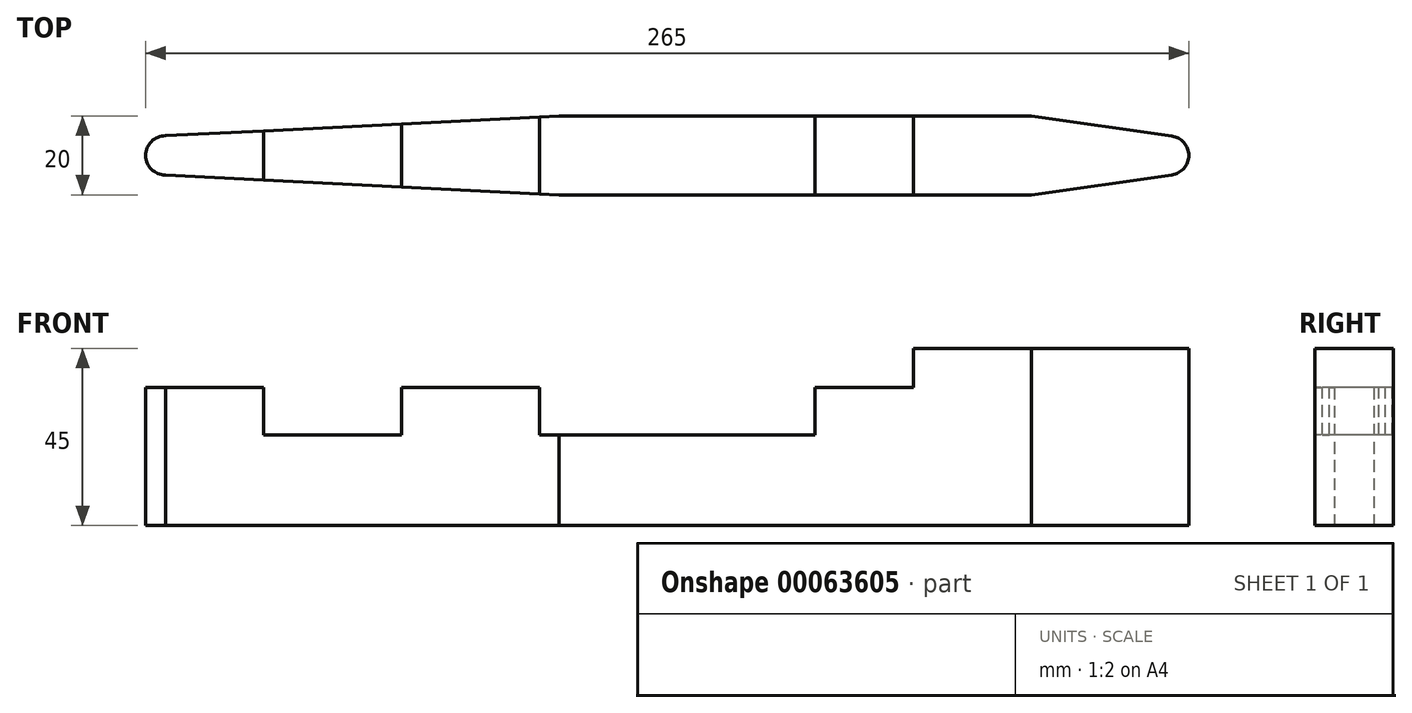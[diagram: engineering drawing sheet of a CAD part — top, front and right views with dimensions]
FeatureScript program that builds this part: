
annotation { "Feature Type Name" : "Feature", "Feature Type Description" : "" }
export const myFeature = defineFeature(function(context is Context, id is Id, definition is map)
    precondition{}
    {
        {
            var Q0;
            Q0=qCreatedBy(makeId("Top.planeOp"),FACE);
            var sketch = newSketch(context, id + "F0", { "sketchPlane" : qUnion([Q0])});
            skLineSegment(sketch, "E0.bottom", {"start": v(57.18, -9.81) * mm, "end": v(-62.82, -9.81) * mm});
            skPoint(sketch, "E0.middle", {"position": v(-35.32, 0.19) * mm});
            skLineSegment(sketch, "E1", {"start": v(-167.82, 0.19) * mm, "end": v(97.18, 0.19) * mm, "construction": true});
            skLineSegment(sketch, "E2", {"start": v(-62.82, 17.45) * mm, "end": v(-62.82, -22.54) * mm, "construction": true});
            skLineSegment(sketch, "E3", {"start": v(57.18, 19.18) * mm, "end": v(57.18, -20.82) * mm, "construction": true});
            skArc(sketch, "E4", {"start": v(-162.82, 5.19) * mm, "mid": v(-167.82, 0.19) * mm, "end": v(-162.82, -4.81) * mm});
            skLineSegment(sketch, "E5", {"start": v(-62.82, -9.81) * mm, "end": v(-162.82, -4.81) * mm});
            skLineSegment(sketch, "E6", {"start": v(57.18, 10.19) * mm, "end": v(92.88, 5.14) * mm});
            skLineSegment(sketch, "E7", {"start": v(57.18, -9.81) * mm, "end": v(92.88, -4.76) * mm});
            skPoint(sketch, "E8.orphan", {"position": v(97.18, 10.19) * mm});
            skPoint(sketch, "E9.orphan", {"position": v(97.18, -9.81) * mm});
            skLineSegment(sketch, "E10", {"start": v(57.18, 10.19) * mm, "end": v(-62.82, 10.19) * mm});
            skLineSegment(sketch, "E11", {"start": v(-62.82, 10.19) * mm, "end": v(-162.82, 5.19) * mm});
            skPoint(sketch, "E12.orphan", {"position": v(-167.82, 10.19) * mm});
            skPoint(sketch, "E0.right.start.orphan", {"position": v(-167.82, -9.81) * mm});
            skLineSegment(sketch, "E13.trimOffspring", {"start": v(92.18, -4.81) * mm, "end": v(92.18, -4.86) * mm, "construction": true});
            skLineSegment(sketch, "E14", {"start": v(92.18, -4.86) * mm, "end": v(92.88, -4.76) * mm});
            skLineSegment(sketch, "E15", {"start": v(97.18, 4.48) * mm, "end": v(97.18, 0.19) * mm});
            skLineSegment(sketch, "E16", {"start": v(97.18, 4.48) * mm, "end": v(97.18, 4.53) * mm});
            skArc(sketch, "E17", {"start": v(92.88, -4.76) * mm, "mid": v(97.18, 0.19) * mm, "end": v(92.88, 5.14) * mm});
            skPoint(sketch, "E18.orphan", {"position": v(92.18, -8.18) * mm});
            skSolve(sketch);
        }
        {
            var Q0;
            Q0=makeQuery(id+"F0.imprint","IMPRINT",FACE,{"disambiguationData":[TD([[makeQuery(id+"F0.imprint","IMPRINT",EDGE,{"derivedFrom":sQuery(id+"F0.wireOp",EDGE,"E0.bottom")}),-1.0]])]});
            extrude(context, id + "F1", {"entities" : qUnion([Q0]), "depth" : 35 * mm});
        }
        {
            var Q0;
            Q0=makeQuery(id+"F1.opExtrude","CAP_FACE",FACE,{"disambiguationData":[OSD([sQuery(id+"F0.wireOp",EDGE,"E0.bottom"),sQuery(id+"F0.wireOp",EDGE,"14d6f1a2-3771-4236-a4c2-8c3a8a42184f"),sQuery(id+"F0.wireOp",EDGE,"E4"),sQuery(id+"F0.wireOp",EDGE,"E5"),sQuery(id+"F0.wireOp",EDGE,"E6"),sQuery(id+"F0.wireOp",EDGE,"E7"),sQuery(id+"F0.wireOp",EDGE,"E10"),sQuery(id+"F0.wireOp",EDGE,"E11")])],"isStart":false});
            var sketch = newSketch(context, id + "F2", { "sketchPlane" : qUnion([Q0])});
            skLineSegment(sketch, "E19", {"start": v(27.18, 10.19) * mm, "end": v(27.18, -9.81) * mm, "construction": true});
            skLineSegment(sketch, "E20", {"start": v(27.18, 10.19) * mm, "end": v(27.18, -9.81) * mm});
            skSolve(sketch);
        }
        {
            var Q0;
            {var subQ2=sQuery(id+"F2.wireOp",EDGE,"E20");Q0=makeQuery(id+"F2.imprint","IMPRINT",FACE,{"disambiguationData":[TD([[makeQuery(id+"F2.imprint","IMPRINT",EDGE,{"derivedFrom":subQ2}),1.0]])]});}
            extrude(context, id + "F3", {"entities" : qUnion([Q0]), "operationType" : NewBodyOperationType.ADD, "depth" : 10 * mm});
        }
        {
            var Q0;
            Q0=makeQuery(id+"F1.opExtrude","CAP_FACE",FACE,{"disambiguationData":[OSD([sQuery(id+"F0.wireOp",EDGE,"E0.bottom"),sQuery(id+"F0.wireOp",EDGE,"14d6f1a2-3771-4236-a4c2-8c3a8a42184f"),sQuery(id+"F0.wireOp",EDGE,"E4"),sQuery(id+"F0.wireOp",EDGE,"E5"),sQuery(id+"F0.wireOp",EDGE,"E6"),sQuery(id+"F0.wireOp",EDGE,"E7"),sQuery(id+"F0.wireOp",EDGE,"E10"),sQuery(id+"F0.wireOp",EDGE,"E11")])],"isStart":false});
            var sketch = newSketch(context, id + "F4", { "sketchPlane" : qUnion([Q0])});
            skLineSegment(sketch, "E21", {"start": v(2.18, 10.19) * mm, "end": v(2.18, -9.81) * mm});
            skLineSegment(sketch, "E22", {"start": v(-67.82, 10.19) * mm, "end": v(-67.82, -9.81) * mm});
            skLineSegment(sketch, "E23", {"start": v(-137.82, 6.44) * mm, "end": v(-137.82, -6.06) * mm});
            skLineSegment(sketch, "E24", {"start": v(-102.82, 8.19) * mm, "end": v(-102.82, -7.81) * mm});
            skSolve(sketch);
        }
        {
            var Q0;
            Q0 = qSketchRegion(id + "F4", true);
            var Q1;
            {var subQ9=sQuery(id+"F4.wireOp",EDGE,"E21");Q1=makeQuery(id+"F4.imprint","IMPRINT",FACE,{"disambiguationData":[TD([[makeQuery(id+"F4.imprint","IMPRINT",EDGE,{"derivedFrom":subQ9}),-1.0]])]});}
            extrude(context, id + "F5", {"entities" : qUnion([Q0, Q1]), "operationType" : NewBodyOperationType.REMOVE, "oppositeDirection" : true, "depth" : 12 * mm});
        }
        {
            var Q0;
            {var subQ0=sQuery(id+"F4.wireOp",EDGE,"E23");Q0=makeQuery(id+"F4.imprint","IMPRINT",FACE,{"disambiguationData":[TD([[makeQuery(id+"F4.imprint","IMPRINT",EDGE,{"derivedFrom":subQ0}),1.0]])]});}
            extrude(context, id + "F6", {"entities" : qUnion([Q0]), "operationType" : NewBodyOperationType.REMOVE, "oppositeDirection" : true, "depth" : 12 * mm});
        }
    });
